# Revit family: Festpunkthalterung HV1
name_source: partatom
category: HLS-Bauteile
revit_build: Autodesk Revit 2017 (Build: 20190507_1515(x64)
units: mm (PartAtom-declared; Revit-internal decimal feet)

## family parameters
Arbeitsebenenbasiert = Ja
Beim Laden mit Abzugskörper schneiden = Nein
Bemaßung runder Anschluss = Durchmesser verwenden
Gemeinsam genutzt = Ja
Immer vertikal = Nein
Raumberechnungspunkt = Nein
Teiletyp = Normal

## types (1)
- Festpunkthalterung HV1
    Anzahl Rohrschellen = 2
    Anzugsmoment Hammersperrkopf = 120 Nm
    Artikelnummer = 00200405/fvz
    Breite Material Rohrschelle = 50 mm
    DF1 = 29 mm  [stored 0.0951444 ft]
    DS = 6 mm  [stored 0.019685 ft]
    EAN = 4250928400000
    Fabrikat = MEFA
    Firma = MEFA Befestigungs- und Montagesysteme GmbH
    Gewicht = 3.58 kg
    Gewicht pro Bauteil = 3.58 kg
    H1 = 100 mm  [stored 0.328084 ft]
    Kurztext1 = Festpunkthalterung HV 1
    Kurztext2 = 64 - 273 mm Fx 20 kN 111 - 163 mm
    L = 120 mm  [stored 0.393701 ft]
    L1 = 35 mm  [stored 0.114829 ft]
    L2 = 25 mm  [stored 0.082021 ft]
    Langloch = Langloch 14 x 20
    Länge = 120 mm  [stored 0.393701 ft]
    Material = Stahl
    Materialname = S235
    Mengeneinheit = St
    Oberflaeche = feuerstückverzinkt
    Rohrschellentyp = Titan HD
    Stärke Material Rohrschelle = 5 mm
    Vorgabe-Ansicht = 1219 mm
    Werte im Brandfall vorhanden = 120/6/100 mm
    Winkel Seitenteil = 120/6/100 mm
    Winkel gedreht = Winkel 120-6-100 für HV1, gedreht
    max. Achshöhe = 163 mm
    max. Rohraußendurchmesser = 273 mm  [stored 0.895669 ft]
    max. zul. Last Fx = 20.00 kN
    max. zul. Last Fz = 12.00 kN
    min. Achshöhe = 111 mm
    min. Rohraußendurchmesser = 64 mm  [stored 0.209974 ft]
    vpe = 1 St

note: [stored X ft] marks values corroborated as IEEE doubles in the binary element streams (Revit-internal decimal feet)

## geometry (parser evidence)
native form markers: Sweep x3
no freeform markers — native parametric forms only
